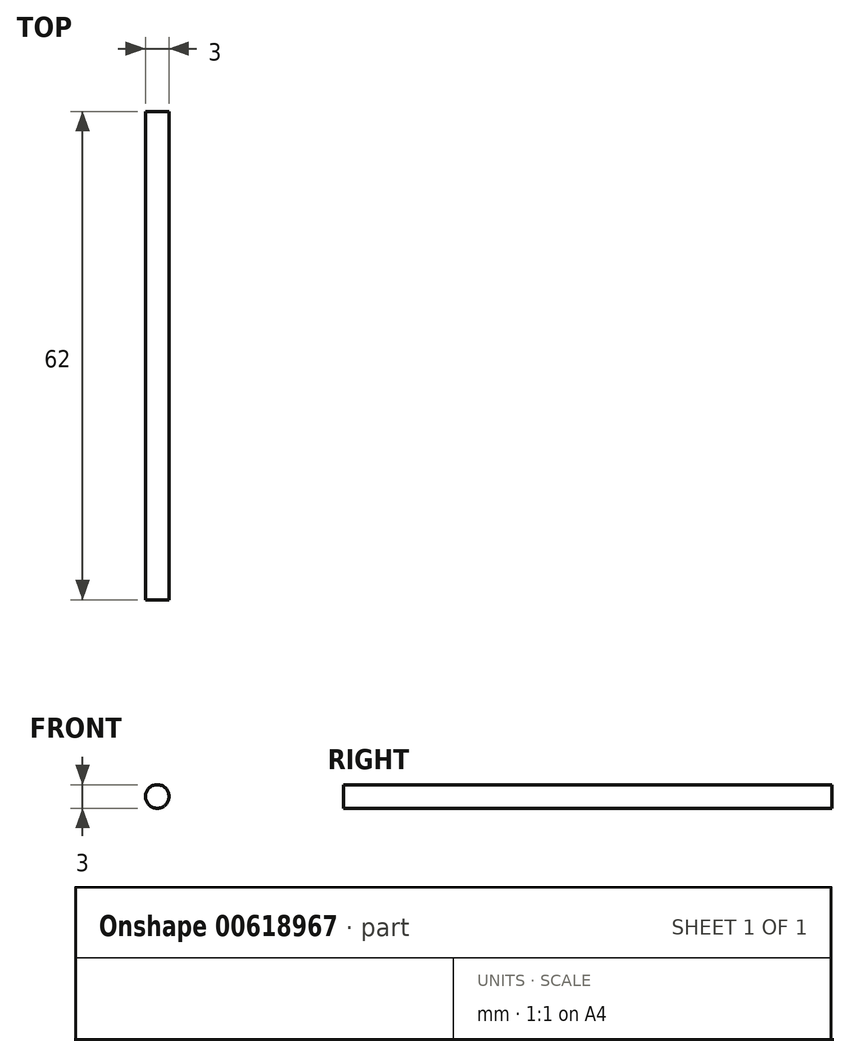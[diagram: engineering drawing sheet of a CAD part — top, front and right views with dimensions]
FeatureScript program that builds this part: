
annotation { "Feature Type Name" : "Feature", "Feature Type Description" : "" }
export const myFeature = defineFeature(function(context is Context, id is Id, definition is map)
    precondition{}
    {
        {
            var Q0;
            Q0=qCreatedBy(makeId("Front.planeOp"),FACE);
            var sketch = newSketch(context, id + "F0", { "sketchPlane" : qUnion([Q0])});
            skCircle(sketch, "E0", {"center": v(0, 0) * mm, "radius": 1.5 * mm});
            skSolve(sketch);
        }
        {
            var Q0;
            Q0 = qSketchRegion(id + "F0", true);
            extrude(context, id + "F1", {"entities" : qUnion([Q0]), "endBound" : BoundingType.SYMMETRIC, "depth" : 62 * mm, "offsetDistance" : 25 * mm});
        }
    });
